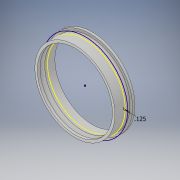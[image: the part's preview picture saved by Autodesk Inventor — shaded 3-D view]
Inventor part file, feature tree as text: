
AUTODESK INVENTOR PART (.ipt)
format: ipt  version: 2018 (Build 220112000, 112)  size: 148,480 bytes
history: native  units: in
note: dims shown in document units (in); Inventor stores cm internally (conversion verified against a paired STEP export)
features: sketch x3, extrude x2, revolve x1, projected_geometry x1
ambient origin geometry x8: Origin, YZ Plane, XZ Plane, XY Plane, X Axis, Y Axis, Z Axis, Center Point
bodies: Solid1 (feature_tree)
feature tree (7):
  revolve  "Revolution1"  [1 undecoded]
  sketch  "Sketch2"  dims[d3=0.25in d4=0.25in]
  extrude  "Extrusion1"  Depth=0.25in
  extrude  "Extrusion2"  Depth=0.135in
  sketch  "Sketch1"  dims[d1=1.875in d2=0.124in]
  projected_geometry  "Projected Loop1"
  sketch  "Sketch3"  dims[d5=0.0675in d6=0.135in d7=90.0deg d8=0.125in d9=0.25in d10=0.0in d11=0.125in d12=0.0in]
note: 1 required parameter value undecoded (feature->parameter linkage not recoverable at this tier; creation-order binding heuristic only, values carry confidence <= 0.55)
